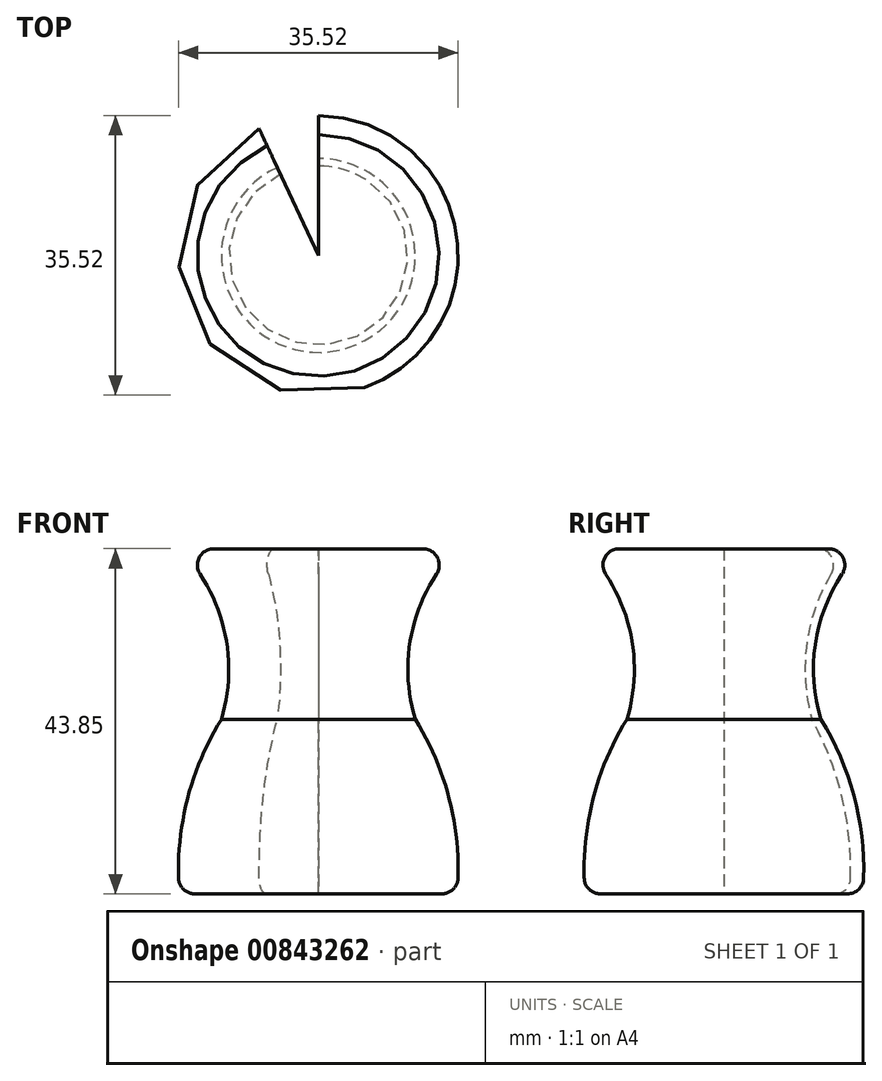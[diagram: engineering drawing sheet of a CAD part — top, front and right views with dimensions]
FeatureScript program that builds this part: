
annotation { "Feature Type Name" : "Feature", "Feature Type Description" : "" }
export const myFeature = defineFeature(function(context is Context, id is Id, definition is map)
    precondition{}
    {
        {
            var Q0;
            Q0=qCreatedBy(makeId("Right.planeOp"),FACE);
            var sketch = newSketch(context, id + "F0", { "sketchPlane" : qUnion([Q0])});
            skLineSegment(sketch, "E0", {"start": v(0, 43.85) * mm, "end": v(17.64, 43.85) * mm});
            skArc(sketch, "E1", {"start": v(17.64, 43.85) * mm, "mid": v(12, 33.74) * mm, "end": v(12.32, 22.17) * mm});
            skArc(sketch, "E2", {"start": v(17.64, 0) * mm, "mid": v(16.76, 11.51) * mm, "end": v(12.32, 22.17) * mm});
            skLineSegment(sketch, "E3", {"start": v(0, 0) * mm, "end": v(17.64, 0) * mm});
            skLineSegment(sketch, "E4", {"start": v(0, 43.85) * mm, "end": v(0, 0) * mm});
            skSolve(sketch);
        }
        {
            var Q0;
            Q0=makeQuery(id+"F0.imprint","IMPRINT",FACE,{"disambiguationData":[TD([[makeQuery(id+"F0.imprint","IMPRINT",EDGE,{"derivedFrom":sQuery(id+"F0.wireOp",EDGE,"E0")}),-1.0]])]});
            var Q1;
            Q1=sQuery(id+"F0.wireOp",EDGE,"E4");
            var Q2;
            Q2=sQuery(id+"F0.wireOp",EDGE,"E1");
            var Q3;
            Q3=sQuery(id+"F0.wireOp",EDGE,"E0");
            var Q4;
            Q4=sQuery(id+"F0.wireOp",EDGE,"E2");
            var Q5;
            Q5=sQuery(id+"F0.wireOp",EDGE,"E3");
            var Q6;
            Q6=sQuery(id+"F0.wireOp",EDGE,"E4");
            revolve(context, id + "F1", {"surfaceOperationType" : NewSurfaceOperationType.ADD, "entities" : qUnion([Q0]), "surfaceEntities" : qUnion([Q1, Q2, Q3, Q4, Q5]), "axis" : qUnion([Q6]), "revolveType" : RevolveType.ONE_DIRECTION, "angle" : 335 * degree});
        }
        {
            var Q0;
            Q0=makeQuery(id+"F1.opRevolve","SWEPT_EDGE",EDGE,{"disambiguationData":[OSD([sQuery(id+"F0.wireOp",EDGE,"E0"),sQuery(id+"F0.wireOp",EDGE,"E1")])]});
            var Q1;
            Q1=makeQuery(id+"F1.opRevolve","SWEPT_EDGE",EDGE,{"disambiguationData":[OSD([sQuery(id+"F0.wireOp",EDGE,"E2"),sQuery(id+"F0.wireOp",EDGE,"E3")])]});
            fillet(context, id + "F2", {"entities" : qUnion([Q0, Q1]), "radius" : 2.08 * mm, "tangentPropagation" : true, "allowEdgeOverflow" : false});
        }
    });
